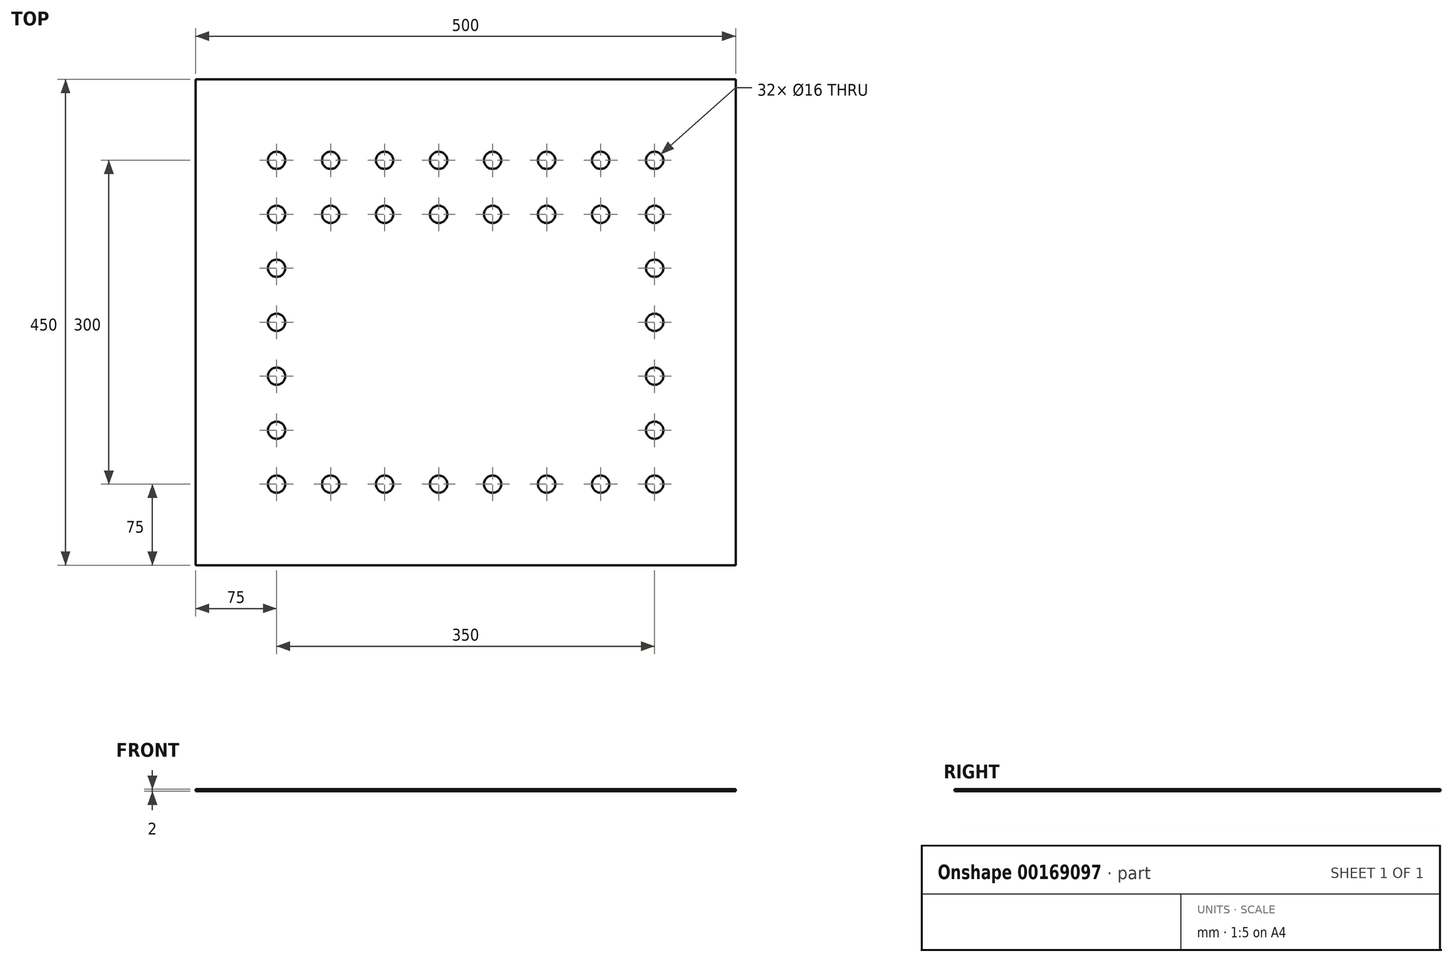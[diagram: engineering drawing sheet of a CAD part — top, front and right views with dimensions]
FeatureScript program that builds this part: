
annotation { "Feature Type Name" : "Feature", "Feature Type Description" : "" }
export const myFeature = defineFeature(function(context is Context, id is Id, definition is map)
    precondition{}
    {
        {
            var Q0;
            Q0=qCreatedBy(makeId("Top.planeOp"),FACE);
            var sketch = newSketch(context, id + "F0", { "sketchPlane" : qUnion([Q0])});
            skLineSegment(sketch, "E0.bottom", {"start": v(250, 225) * mm, "end": v(-250, 225) * mm});
            skLineSegment(sketch, "E0.top", {"start": v(250, -225) * mm, "end": v(-250, -225) * mm});
            skLineSegment(sketch, "E0.left", {"start": v(250, 225) * mm, "end": v(250, -225) * mm});
            skLineSegment(sketch, "E0.right", {"start": v(-250, 225) * mm, "end": v(-250, -225) * mm});
            skPoint(sketch, "E0.middle", {"position": v(0, 0) * mm});
            skLineSegment(sketch, "E1.bottom", {"start": v(175, 150) * mm, "end": v(-175, 150) * mm, "construction": true});
            skLineSegment(sketch, "E1.top", {"start": v(175, -150) * mm, "end": v(-175, -150) * mm, "construction": true});
            skLineSegment(sketch, "E1.left", {"start": v(175, 150) * mm, "end": v(175, -150) * mm, "construction": true});
            skLineSegment(sketch, "E1.right", {"start": v(-175, 150) * mm, "end": v(-175, -150) * mm, "construction": true});
            skCircle(sketch, "E2", {"center": v(-175, 150) * mm, "radius": 8 * mm});
            skLineSegment(sketch, "E3.1.0.0", {"start": v(225, 150) * mm, "end": v(-125, 150) * mm, "construction": true});
            skCircle(sketch, "E3.1.0.1", {"center": v(-125, 150) * mm, "radius": 8 * mm});
            skLineSegment(sketch, "E3.2.0.0", {"start": v(275, 150) * mm, "end": v(-75, 150) * mm, "construction": true});
            skCircle(sketch, "E3.2.0.1", {"center": v(-75, 150) * mm, "radius": 8 * mm});
            skLineSegment(sketch, "E3.3.0.0", {"start": v(325, 150) * mm, "end": v(-25, 150) * mm, "construction": true});
            skCircle(sketch, "E3.3.0.1", {"center": v(-25, 150) * mm, "radius": 8 * mm});
            skLineSegment(sketch, "E3.4.0.0", {"start": v(375, 150) * mm, "end": v(25, 150) * mm, "construction": true});
            skCircle(sketch, "E3.4.0.1", {"center": v(25, 150) * mm, "radius": 8 * mm});
            skLineSegment(sketch, "E3.5.0.0", {"start": v(425, 150) * mm, "end": v(75, 150) * mm, "construction": true});
            skCircle(sketch, "E3.5.0.1", {"center": v(75, 150) * mm, "radius": 8 * mm});
            skLineSegment(sketch, "E3.6.0.0", {"start": v(475, 150) * mm, "end": v(125, 150) * mm, "construction": true});
            skCircle(sketch, "E3.6.0.1", {"center": v(125, 150) * mm, "radius": 8 * mm});
            skLineSegment(sketch, "E3.7.0.0", {"start": v(525, 150) * mm, "end": v(175, 150) * mm, "construction": true});
            skCircle(sketch, "E3.7.0.1", {"center": v(175, 150) * mm, "radius": 8 * mm});
            skLineSegment(sketch, "E3.direction1", {"start": v(-175, 150) * mm, "end": v(-125, 150) * mm, "construction": true});
            skLineSegment(sketch, "E4", {"start": v(0, 0) * mm, "end": v(325.44, 0) * mm, "construction": true});
            skLineSegment(sketch, "E5.MirrorCS", {"start": v(525, -150) * mm, "end": v(175, -150) * mm, "construction": true});
            skLineSegment(sketch, "E6.MirrorCS", {"start": v(475, -150) * mm, "end": v(125, -150) * mm, "construction": true});
            skLineSegment(sketch, "E7.MirrorCS", {"start": v(325, -150) * mm, "end": v(-25, -150) * mm, "construction": true});
            skLineSegment(sketch, "E8.MirrorCS", {"start": v(425, -150) * mm, "end": v(75, -150) * mm, "construction": true});
            skLineSegment(sketch, "E9.MirrorCS", {"start": v(375, -150) * mm, "end": v(25, -150) * mm, "construction": true});
            skCircle(sketch, "E10.MirrorC", {"center": v(25, -150) * mm, "radius": 8 * mm});
            skCircle(sketch, "E11.MirrorC", {"center": v(-25, -150) * mm, "radius": 8 * mm});
            skLineSegment(sketch, "E12.MirrorCS", {"start": v(250, -225) * mm, "end": v(250, 225) * mm});
            skLineSegment(sketch, "E13.MirrorCS", {"start": v(-250, -225) * mm, "end": v(-250, 225) * mm});
            skCircle(sketch, "E14.MirrorC", {"center": v(125, -150) * mm, "radius": 8 * mm});
            skLineSegment(sketch, "E15.MirrorCS", {"start": v(-175, -150) * mm, "end": v(-125, -150) * mm, "construction": true});
            skCircle(sketch, "E16.MirrorC", {"center": v(-75, -150) * mm, "radius": 8 * mm});
            skLineSegment(sketch, "E17.MirrorCS", {"start": v(-175, -150) * mm, "end": v(-175, 150) * mm, "construction": true});
            skCircle(sketch, "E18.MirrorC", {"center": v(175, -150) * mm, "radius": 8 * mm});
            skCircle(sketch, "E19.MirrorC", {"center": v(-175, -150) * mm, "radius": 8 * mm});
            skLineSegment(sketch, "E20.MirrorCS", {"start": v(175, -150) * mm, "end": v(175, 150) * mm, "construction": true});
            skLineSegment(sketch, "E21.MirrorCS", {"start": v(225, -150) * mm, "end": v(-125, -150) * mm, "construction": true});
            skCircle(sketch, "E22.MirrorC", {"center": v(75, -150) * mm, "radius": 8 * mm});
            skLineSegment(sketch, "E23.MirrorCS", {"start": v(275, -150) * mm, "end": v(-75, -150) * mm, "construction": true});
            skCircle(sketch, "E24.MirrorC", {"center": v(-125, -150) * mm, "radius": 8 * mm});
            skCircle(sketch, "E25.0.1.0", {"center": v(175, -100) * mm, "radius": 8 * mm});
            skCircle(sketch, "E25.0.2.0", {"center": v(175, -50) * mm, "radius": 8 * mm});
            skCircle(sketch, "E25.0.3.0", {"center": v(175, 0) * mm, "radius": 8 * mm});
            skCircle(sketch, "E25.0.4.0", {"center": v(175, 50) * mm, "radius": 8 * mm});
            skCircle(sketch, "E25.0.5.0", {"center": v(175, 100) * mm, "radius": 8 * mm});
            skLineSegment(sketch, "E25.direction1", {"start": v(175, -150) * mm, "end": v(200, -150) * mm, "construction": true});
            skLineSegment(sketch, "E25.direction2", {"start": v(175, -150) * mm, "end": v(175, -100) * mm, "construction": true});
            skLineSegment(sketch, "E26", {"start": v(0, 0) * mm, "end": v(0, 91.67) * mm, "construction": true});
            skLineSegment(sketch, "E27.MirrorCS", {"start": v(-175, -150) * mm, "end": v(-175, -100) * mm, "construction": true});
            skCircle(sketch, "E28.MirrorC", {"center": v(-175, 50) * mm, "radius": 8 * mm});
            skCircle(sketch, "E29.MirrorC", {"center": v(-175, 100) * mm, "radius": 8 * mm});
            skCircle(sketch, "E30.MirrorC", {"center": v(-175, -100) * mm, "radius": 8 * mm});
            skCircle(sketch, "E31.MirrorC", {"center": v(-175, 0) * mm, "radius": 8 * mm});
            skLineSegment(sketch, "E32.MirrorCS", {"start": v(0, 0) * mm, "end": v(-325.44, 0) * mm, "construction": true});
            skCircle(sketch, "E33.MirrorC", {"center": v(-175, -50) * mm, "radius": 8 * mm});
            skCircle(sketch, "E34.1.0.0", {"center": v(-125, 100) * mm, "radius": 8 * mm});
            skCircle(sketch, "E34.2.0.0", {"center": v(-75, 100) * mm, "radius": 8 * mm});
            skCircle(sketch, "E34.3.0.0", {"center": v(-25, 100) * mm, "radius": 8 * mm});
            skCircle(sketch, "E34.4.0.0", {"center": v(25, 100) * mm, "radius": 8 * mm});
            skCircle(sketch, "E34.5.0.0", {"center": v(75, 100) * mm, "radius": 8 * mm});
            skCircle(sketch, "E34.6.0.0", {"center": v(125, 100) * mm, "radius": 8 * mm});
            skLineSegment(sketch, "E34.direction1", {"start": v(-175, 100) * mm, "end": v(-125, 100) * mm, "construction": true});
            skSolve(sketch);
        }
        {
            var Q0;
            Q0=qSketchRegion(id+"F0",true);
            extrude(context, id + "F1", {"entities" : qUnion([Q0]), "depth" : 2 * mm});
        }
    });
